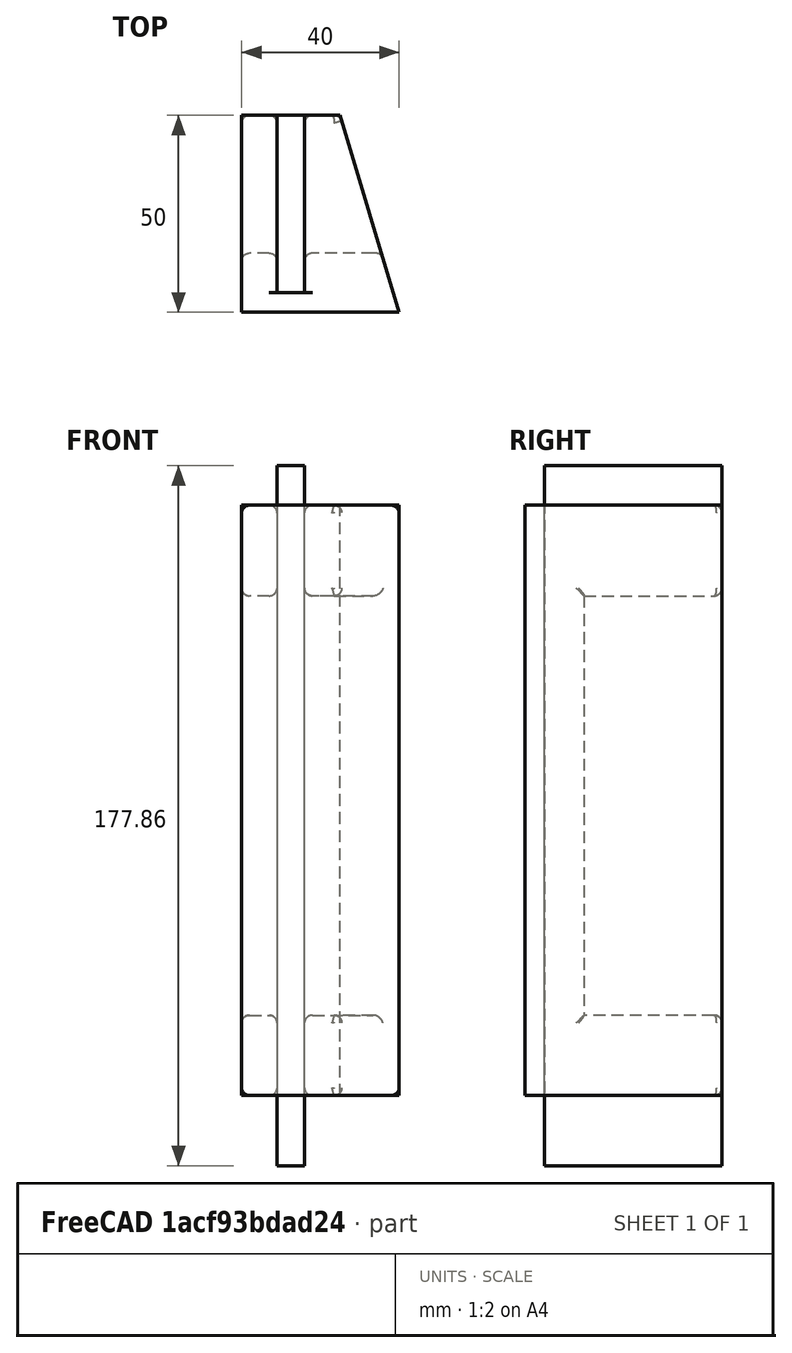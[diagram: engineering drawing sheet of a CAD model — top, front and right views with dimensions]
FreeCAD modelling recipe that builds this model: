
FCSTD DOCUMENT  (FreeCAD 0.16R)
Label: ScaleHolder
License: All rights reserved
LicenseURL: http://en.wikipedia.org/wiki/All_rights_reserved
objects: Sketcher::SketchObject×3, PartDesign::Fillet×3, PartDesign::Pocket×2, PartDesign::Pad×1, Mesh::Feature×1
note: 12 computed .brp shape members not serialized (recipe doc carries the construction recipe); baked Part::Feature solids carry a one-line shape summary decoded from their .brp

FEATURE [Sketcher::SketchObject] Sketch
  sketch-geometry (4):
    g0: LineSegment StartX=0 StartY=50 StartZ=0 EndX=0 EndY=0 EndZ=0
    g1: LineSegment StartX=0 StartY=0 StartZ=0 EndX=40 EndY=0 EndZ=0
    g2: LineSegment StartX=40 StartY=0 StartZ=0 EndX=25 EndY=50 EndZ=0
    g3: LineSegment StartX=25 StartY=50 StartZ=0 EndX=0 EndY=50 EndZ=0
  constraints (11):
    c: PointOnObject(g0,g-2)
    c: Coincident(g0,g-1)
    c: Coincident(g0,g1)
    c: PointOnObject(g1,g-1)
    c: Coincident(g1,g2)
    c: Coincident(g2,g3)
    c: Coincident(g3,g0)
    c: Horizontal(g3)
    c: Distance(g3) = 25
    c: Distance(g1) = 40
    c: Distance(g0) = 50
FEATURE [PartDesign::Pad] Pad
  Length = 150
  Length2 = 100
  Sketch = -> Sketch
  Type = 0
FEATURE [Sketcher::SketchObject] Sketch001
  ExternalGeometry = -> [Pad]
  Placement = pos=(0,50,0) rot=(0,0.707107,0.707107;3.14159rad)
  Support = -> Pad [Face4]
  sketch-geometry (5):
    g0: LineSegment StartX=-16 StartY=160.054 StartZ=0 EndX=-9 EndY=160.054 EndZ=0
    g1: LineSegment StartX=-9 StartY=160.054 StartZ=0 EndX=-9 EndY=-17.814 EndZ=0
    g2: LineSegment StartX=-9 StartY=-17.814 StartZ=0 EndX=-16 EndY=-17.814 EndZ=0
    g3: LineSegment StartX=-16 StartY=-17.814 StartZ=0 EndX=-16 EndY=160.054 EndZ=0
    g4: LineSegment [constr] StartX=-12.5 StartY=173.555 StartZ=0 EndX=-12.5 EndY=-54.4991 EndZ=0
  constraints (12):
    c: Coincident(g0,g1)
    c: Coincident(g1,g2)
    c: Coincident(g2,g3)
    c: Coincident(g3,g0)
    c: Horizontal(g0)
    c: Horizontal(g2)
    c: Vertical(g1)
    c: Vertical(g3)
    c: Distance(g0) = 7
    c: Vertical(g4)
    c: Symmetric(g0,g0,g4)
    c: Symmetric(g-3,g-1,g4)
FEATURE [PartDesign::Pocket] Pocket
  Length = 45
  Sketch = -> Sketch001
  Type = 0
FEATURE [Sketcher::SketchObject] Sketch002
  Placement = pos=(0,50,0) rot=(0,0.707107,0.707107;3.14159rad)
  Support = -> Pocket [Face2]
  sketch-geometry (4):
    g0: LineSegment StartX=-89.6048 StartY=126.947 StartZ=0 EndX=50.7096 EndY=126.947 EndZ=0
    g1: LineSegment StartX=50.7096 StartY=126.947 StartZ=0 EndX=50.7096 EndY=20.4304 EndZ=0
    g2: LineSegment StartX=50.7096 StartY=20.4304 StartZ=0 EndX=-89.6048 EndY=20.4304 EndZ=0
    g3: LineSegment StartX=-89.6048 StartY=20.4304 StartZ=0 EndX=-89.6048 EndY=126.947 EndZ=0
  constraints (8):
    c: Coincident(g0,g1)
    c: Coincident(g1,g2)
    c: Coincident(g2,g3)
    c: Coincident(g3,g0)
    c: Horizontal(g0)
    c: Horizontal(g2)
    c: Vertical(g1)
    c: Vertical(g3)
FEATURE [PartDesign::Pocket] Pocket001
  Length = 35
  Sketch = -> Sketch002
  Type = 0
FEATURE [PartDesign::Fillet] Fillet
  Base = -> Pocket001 [Edge14,Edge12,Edge10,Edge1,Edge5,Edge27,Edge38,Edge44,Edge23,Edge42,Edge7,Edge3,Edge19,Edge21,Edge36,Edge31]
  Radius = 2
FEATURE [PartDesign::Fillet] Fillet001
  Base = -> Fillet [Edge88,Edge89,Edge90,Edge67,Edge91,Edge62,Edge92,Edge57,Edge28,Edge29,Edge30,Edge31,Edge5,Edge32,Edge20,Edge33,Edge22,Edge23,Edge18,Edge24,Edge4,Edge25,Edge26,Edge27,Edge50,Edge60,Edge82,Edge63,Edge83,Edge84,Edge85,Edge86]
  Radius = 2
FEATURE [PartDesign::Fillet] Fillet002
  Base = -> Fillet001 [Edge74,Edge135,Edge31,Edge8]
  Radius = 2
FEATURE [Mesh::Feature] Mesh  label="Fillet002 (Meshed)"
